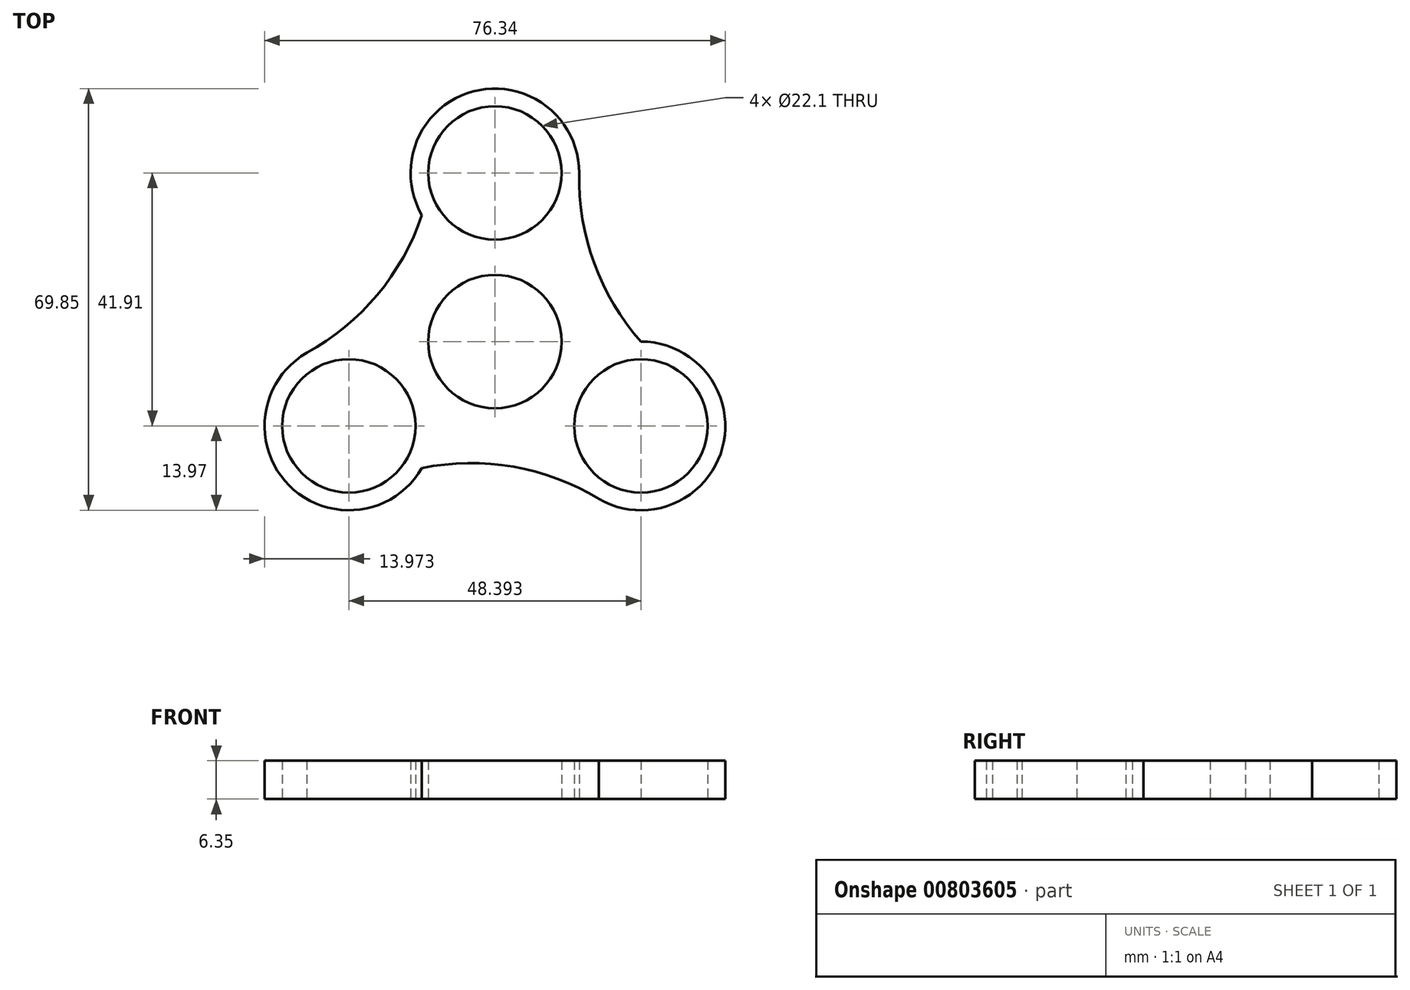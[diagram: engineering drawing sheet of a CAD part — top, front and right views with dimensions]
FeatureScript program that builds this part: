
annotation { "Feature Type Name" : "Feature", "Feature Type Description" : "" }
export const myFeature = defineFeature(function(context is Context, id is Id, definition is map)
    precondition{}
    {
        {
            var Q0;
            Q0=qCreatedBy(makeId("Top.planeOp"),FACE);
            var sketch = newSketch(context, id + "F0", { "sketchPlane" : qUnion([Q0])});
            skCircle(sketch, "E0", {"center": v(0, 0) * mm, "radius": 44.45 * mm});
            skCircle(sketch, "E1", {"center": v(0, 0) * mm, "radius": 11.05 * mm});
            skLineSegment(sketch, "E2", {"start": v(0, 0) * mm, "end": v(0, 27.94) * mm});
            skCircle(sketch, "E3", {"center": v(0, 27.94) * mm, "radius": 11.05 * mm});
            skCircle(sketch, "E4.1.0", {"center": v(-24.2, -13.97) * mm, "radius": 11.05 * mm});
            skCircle(sketch, "E4.2.0", {"center": v(24.2, -13.97) * mm, "radius": 11.05 * mm});
            skSolve(sketch);
        }
        {
            var Q0;
            Q0=makeQuery(id+"F0.imprint","IMPRINT",FACE,{"disambiguationData":[TD([[makeQuery(id+"F0.imprint","IMPRINT",EDGE,{"derivedFrom":sQuery(id+"F0.wireOp",EDGE,"E0")}),1.0]])]});
            var sketch = newSketch(context, id + "F1", { "sketchPlane" : qUnion([Q0])});
            skCircle(sketch, "E5", {"center": v(0, 27.94) * mm, "radius": 13.97 * mm});
            skCircle(sketch, "E6.1.0", {"center": v(-24.2, -13.97) * mm, "radius": 13.97 * mm});
            skCircle(sketch, "E6.2.0", {"center": v(24.2, -13.97) * mm, "radius": 13.97 * mm});
            skPoint(sketch, "E6.center", {"position": v(0, 0) * mm});
            skCircle(sketch, "E7", {"center": v(0, 0) * mm, "radius": 13.97 * mm});
            skArc(sketch, "E8", {"start": v(13.97, 27.94) * mm, "mid": v(16.44, 13) * mm, "end": v(24.2, 0) * mm});
            skArc(sketch, "E9.1.0", {"start": v(17.21, -26.07) * mm, "mid": v(3.04, -20.74) * mm, "end": v(-12.1, -20.95) * mm});
            skArc(sketch, "E9.2.0", {"start": v(-31.18, -1.87) * mm, "mid": v(-19.48, 7.74) * mm, "end": v(-12.1, 20.95) * mm});
            skLineSegment(sketch, "E9.anchor1", {"start": v(0, 0) * mm, "end": v(24.2, 0) * mm, "construction": true});
            skLineSegment(sketch, "E9.anchor2", {"start": v(0, 0) * mm, "end": v(-12.1, 20.95) * mm, "construction": true});
            skSolve(sketch);
        }
        {
            var Q0;
            {var subQ0=sQuery(id+"F1.wireOp",EDGE,"E9.1.0");var subQ1=sQuery(id+"F1.wireOp",EDGE,"E6.1.0");var subQ2=makeQuery(id+"F1.imprint","INTERSECT",VERTEX,{"derivedFrom":[subQ1,subQ0]});Q0=makeQuery(id+"F1.imprint","IMPRINT",FACE,{"disambiguationData":[TD([[makeQuery(id+"F1.imprint","IMPRINT",EDGE,{"disambiguationData":[TD([[subQ2,-1.0]])],"derivedFrom":subQ1}),-1.0]])]});}
            var Q1;
            {var subQ0=sQuery(id+"F1.wireOp",EDGE,"E9.2.0");var subQ1=sQuery(id+"F1.wireOp",EDGE,"E5");var subQ2=makeQuery(id+"F1.imprint","INTERSECT",VERTEX,{"derivedFrom":[subQ1,subQ0]});Q1=makeQuery(id+"F1.imprint","IMPRINT",FACE,{"disambiguationData":[TD([[makeQuery(id+"F1.imprint","IMPRINT",EDGE,{"disambiguationData":[TD([[subQ2,-1.0]])],"derivedFrom":subQ1}),-1.0]])]});}
            var Q2;
            {var subQ0=sQuery(id+"F1.wireOp",EDGE,"E7");var subQ1=sQuery(id+"F1.wireOp",EDGE,"E5");var subQ2=makeQuery(id+"F1.imprint","INTERSECT",VERTEX,{"derivedFrom":[subQ1,subQ0]});Q2=makeQuery(id+"F1.imprint","IMPRINT",FACE,{"disambiguationData":[TD([[makeQuery(id+"F1.imprint","IMPRINT",EDGE,{"disambiguationData":[TD([[subQ2,-1.0]])],"derivedFrom":subQ1}),-1.0]])]});}
            var Q3;
            Q3=makeQuery(id+"F1.imprint","IMPRINT",FACE,{"disambiguationData":[TD([[makeQuery(id+"F1.imprint","IMPRINT",EDGE,{"derivedFrom":makeQuery(id+"F0.imprint","IMPRINT",EDGE,{"derivedFrom":sQuery(id+"F0.wireOp",EDGE,"E4.1.0")})}),-1.0]])]});
            var Q4;
            Q4=makeQuery(id+"F1.imprint","IMPRINT",FACE,{"disambiguationData":[TD([[makeQuery(id+"F1.imprint","IMPRINT",EDGE,{"derivedFrom":makeQuery(id+"F0.imprint","IMPRINT",EDGE,{"derivedFrom":sQuery(id+"F0.wireOp",EDGE,"E3")})}),-1.0]])]});
            var Q5;
            Q5=makeQuery(id+"F1.imprint","IMPRINT",FACE,{"disambiguationData":[TD([[makeQuery(id+"F1.imprint","IMPRINT",EDGE,{"derivedFrom":makeQuery(id+"F0.imprint","IMPRINT",EDGE,{"derivedFrom":sQuery(id+"F0.wireOp",EDGE,"E4.2.0")})}),-1.0]])]});
            var Q6;
            Q6=makeQuery(id+"F1.imprint","IMPRINT",FACE,{"disambiguationData":[TD([[makeQuery(id+"F1.imprint","IMPRINT",EDGE,{"derivedFrom":makeQuery(id+"F0.imprint","IMPRINT",EDGE,{"derivedFrom":sQuery(id+"F0.wireOp",EDGE,"E1")})}),-1.0]])]});
            extrude(context, id + "F2", {"entities" : qUnion([Q0, Q1, Q2, Q3, Q4, Q5, Q6]), "depth" : 6.35 * mm, "offsetDistance" : 25.4 * mm});
        }
    });
